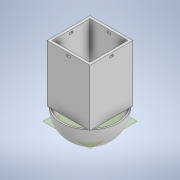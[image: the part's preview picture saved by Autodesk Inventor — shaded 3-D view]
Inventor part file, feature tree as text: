
AUTODESK INVENTOR PART (.ipt)
format: ipt  version: 2022 (Build 260153000, 153)  size: 176,128 bytes
history: native  units: in
note: dims shown in document units (in); Inventor stores cm internally (conversion verified against a paired STEP export)
features: sketch x3, extrude x2, pattern_circular x1, revolve x1, plane x1
ambient origin geometry x8: Origin, YZ Plane, XZ Plane, XY Plane, X Axis, Y Axis, Z Axis, Center Point
bodies: Solid1 (feature_tree)
feature tree (8):
  extrude  "Extrusion1"  Depth=0.1575in
  extrude  "Extrusion2"  Depth=3.5433in TaperAngle=0.0deg
  pattern_circular  "Circular Pattern1"  [2 undecoded]
  revolve  "Revolution1"  [1 undecoded]
  plane  "Work Plane1"
  sketch  "Sketch1"  dims[d0=2.3622in d1=0.1575in]
  sketch  "Sketch2"  dims[d2=0.1575in d3=3.5433in d4=0.0in]
  sketch  "Sketch3"  dims[d5=0.1181in d6=0.1181in d7=0.1969in d8=3.5433in d9=0.0in d10=1.5748in d11=360.0deg d14=0.0984in d15=180.0deg d16=0.8268in d17=1.7165in]
note: 3 required parameter values undecoded (feature->parameter linkage not recoverable at this tier; creation-order binding heuristic only, values carry confidence <= 0.55)